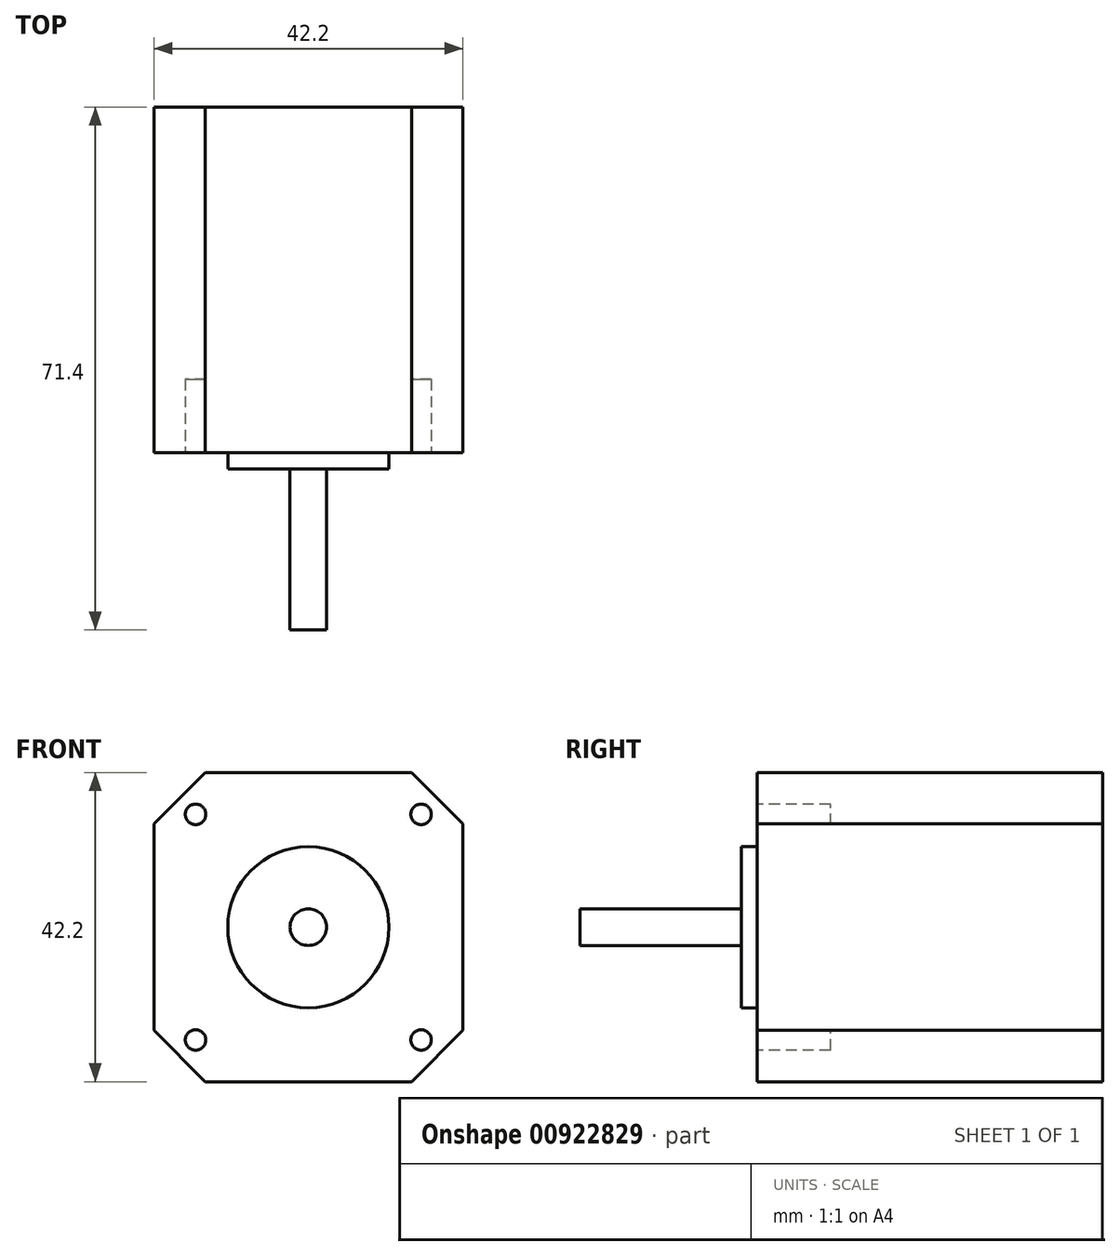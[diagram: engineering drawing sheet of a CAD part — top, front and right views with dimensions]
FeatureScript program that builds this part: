
annotation { "Feature Type Name" : "Feature", "Feature Type Description" : "" }
export const myFeature = defineFeature(function(context is Context, id is Id, definition is map)
    precondition{}
    {
        {
            var Q0;
            Q0=qCreatedBy(makeId("Front.planeOp"),FACE);
            var sketch = newSketch(context, id + "F0", { "sketchPlane" : qUnion([Q0])});
            skLineSegment(sketch, "E0.bottom", {"start": v(-21.1, 21.1) * mm, "end": v(21.1, 21.1) * mm});
            skLineSegment(sketch, "E0.top", {"start": v(-21.1, -21.1) * mm, "end": v(21.1, -21.1) * mm});
            skLineSegment(sketch, "E0.left", {"start": v(-21.1, 21.1) * mm, "end": v(-21.1, -21.1) * mm});
            skLineSegment(sketch, "E0.right", {"start": v(21.1, 21.1) * mm, "end": v(21.1, -21.1) * mm});
            skPoint(sketch, "E0.middle", {"position": v(0, 0) * mm});
            skSolve(sketch);
        }
        {
            var Q0;
            Q0 = qSketchRegion(id + "F0", true);
            extrude(context, id + "F1", {"entities" : qUnion([Q0]), "endBound" : BoundingType.SYMMETRIC, "depth" : 47.2 * mm, "offsetDistance" : 25 * mm});
        }
        {
            var Q0;
            Q0=makeQuery(id+"F1.opExtrude","SWEPT_EDGE",EDGE,{"disambiguationData":[OSD([sQuery(id+"F0.wireOp",EDGE,"E0.bottom"),sQuery(id+"F0.wireOp",EDGE,"E0.right")])]});
            var Q1;
            Q1=makeQuery(id+"F1.opExtrude","SWEPT_EDGE",EDGE,{"disambiguationData":[OSD([sQuery(id+"F0.wireOp",EDGE,"E0.bottom"),sQuery(id+"F0.wireOp",EDGE,"E0.left")])]});
            var Q2;
            Q2=makeQuery(id+"F1.opExtrude","SWEPT_EDGE",EDGE,{"disambiguationData":[OSD([sQuery(id+"F0.wireOp",EDGE,"E0.top"),sQuery(id+"F0.wireOp",EDGE,"E0.right")])]});
            var Q3;
            Q3=makeQuery(id+"F1.opExtrude","SWEPT_EDGE",EDGE,{"disambiguationData":[OSD([sQuery(id+"F0.wireOp",EDGE,"E0.top"),sQuery(id+"F0.wireOp",EDGE,"E0.left")])]});
            chamfer(context, id + "F2", {"entities" : qUnion([Q0, Q1, Q2, Q3]), "width" : 7 * mm, "tangentPropagation" : true});
        }
        {
            var Q0;
            Q0=makeQuery(id+"F1.opExtrude","CAP_FACE",FACE,{"disambiguationData":[OSD([sQuery(id+"F0.wireOp",EDGE,"E0.bottom"),sQuery(id+"F0.wireOp",EDGE,"E0.top"),sQuery(id+"F0.wireOp",EDGE,"E0.left"),sQuery(id+"F0.wireOp",EDGE,"E0.right")])],"isStart":false});
            var sketch = newSketch(context, id + "F3", { "sketchPlane" : qUnion([Q0])});
            skCircle(sketch, "E1", {"center": v(0, 0) * mm, "radius": 2.5 * mm});
            skSolve(sketch);
        }
        {
            var Q0;
            Q0 = qSketchRegion(id + "F3", true);
            extrude(context, id + "F4", {"entities" : qUnion([Q0]), "operationType" : NewBodyOperationType.ADD, "depth" : 24.2 * mm, "offsetDistance" : 25 * mm});
        }
        {
            var Q0;
            Q0=makeQuery(id+"F1.opExtrude","CAP_FACE",FACE,{"disambiguationData":[OSD([sQuery(id+"F0.wireOp",EDGE,"E0.bottom"),sQuery(id+"F0.wireOp",EDGE,"E0.top"),sQuery(id+"F0.wireOp",EDGE,"E0.left"),sQuery(id+"F0.wireOp",EDGE,"E0.right")])],"isStart":false});
            var sketch = newSketch(context, id + "F5", { "sketchPlane" : qUnion([Q0])});
            skCircle(sketch, "E2", {"center": v(0, 0) * mm, "radius": 11 * mm});
            skSolve(sketch);
        }
        {
            var Q0;
            Q0 = qSketchRegion(id + "F5", true);
            extrude(context, id + "F6", {"entities" : qUnion([Q0]), "operationType" : NewBodyOperationType.ADD, "depth" : 2.2 * mm, "offsetDistance" : 25 * mm});
        }
        {
            var Q0;
            Q0=makeQuery(id+"F1.opExtrude","CAP_FACE",FACE,{"disambiguationData":[OSD([sQuery(id+"F0.wireOp",EDGE,"E0.bottom"),sQuery(id+"F0.wireOp",EDGE,"E0.top"),sQuery(id+"F0.wireOp",EDGE,"E0.left"),sQuery(id+"F0.wireOp",EDGE,"E0.right")])],"isStart":false});
            var sketch = newSketch(context, id + "F7", { "sketchPlane" : qUnion([Q0])});
            skLineSegment(sketch, "E3", {"start": v(0, -21.1) * mm, "end": v(0, 0) * mm, "construction": true});
            skLineSegment(sketch, "E4", {"start": v(0, 0) * mm, "end": v(-21.1, 0) * mm, "construction": true});
            skCircle(sketch, "E5", {"center": v(-15.4, -15.4) * mm, "radius": 1.4 * mm});
            skCircle(sketch, "E6.MirrorC", {"center": v(-15.4, 15.4) * mm, "radius": 1.4 * mm});
            skCircle(sketch, "E7.MirrorC", {"center": v(15.4, -15.4) * mm, "radius": 1.4 * mm});
            skCircle(sketch, "E8.MirrorC", {"center": v(15.4, 15.4) * mm, "radius": 1.4 * mm});
            skSolve(sketch);
        }
        {
            var Q0;
            Q0 = qSketchRegion(id + "F7", true);
            extrude(context, id + "F8", {"entities" : qUnion([Q0]), "operationType" : NewBodyOperationType.REMOVE, "oppositeDirection" : true, "depth" : 10 * mm, "offsetDistance" : 25 * mm});
        }
    });
